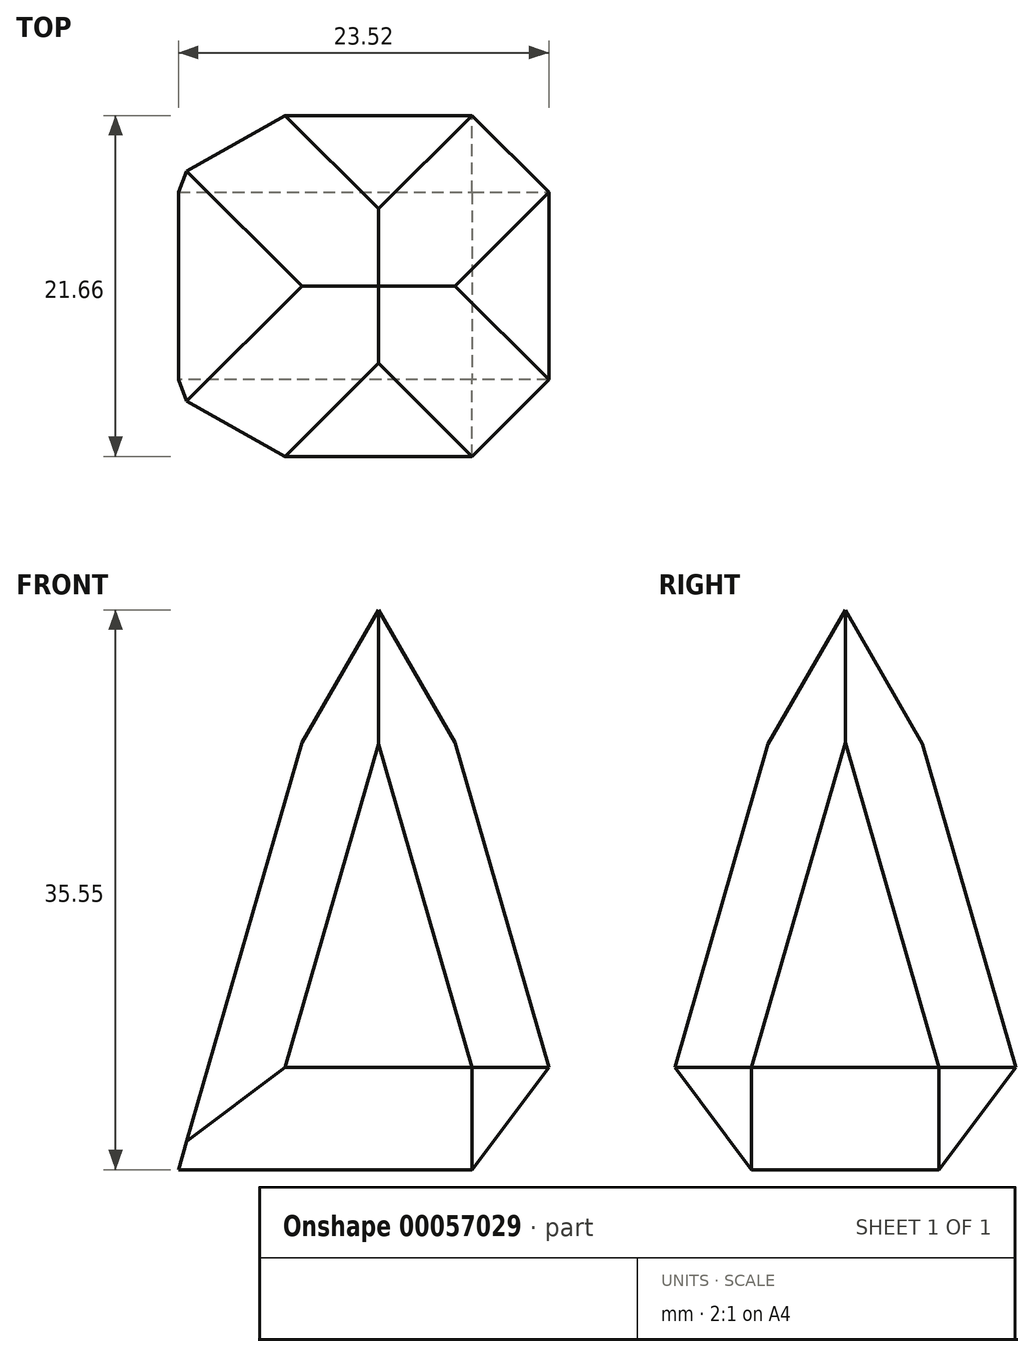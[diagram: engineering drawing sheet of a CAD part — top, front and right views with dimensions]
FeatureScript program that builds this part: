
annotation { "Feature Type Name" : "Feature", "Feature Type Description" : "" }
export const myFeature = defineFeature(function(context is Context, id is Id, definition is map)
    precondition{}
    {
        {
            var Q0;
            Q0=qCreatedBy(makeId("Front.planeOp"),FACE);
            var sketch = newSketch(context, id + "F0", { "sketchPlane" : qUnion([Q0])});
            skLineSegment(sketch, "E0", {"start": v(-12.7, 0) * mm, "end": v(12.7, 0) * mm});
            skLineSegment(sketch, "E1", {"start": v(12.7, 0) * mm, "end": v(0, 43.94) * mm});
            skLineSegment(sketch, "E2", {"start": v(0, 43.94) * mm, "end": v(-12.7, 0) * mm});
            skSolve(sketch);
        }
        {
            var Q0;
            Q0 = qSketchRegion(id + "F0", true);
            extrude(context, id + "F1", {"entities" : qUnion([Q0]), "depth" : 25.4 * mm});
        }
        {
            var Q0;
            Q0=qCreatedBy(makeId("Right.planeOp"),FACE);
            var sketch = newSketch(context, id + "F2", { "sketchPlane" : qUnion([Q0])});
            skLineSegment(sketch, "E3", {"start": v(0, 0) * mm, "end": v(0, 44.07) * mm});
            skLineSegment(sketch, "E4", {"start": v(0, 44.07) * mm, "end": v(-25.4, 44.07) * mm});
            skLineSegment(sketch, "E5", {"start": v(-25.4, 44.07) * mm, "end": v(-25.4, 0) * mm});
            skLineSegment(sketch, "E6", {"start": v(-25.4, 0) * mm, "end": v(-12.7, 44.07) * mm});
            skLineSegment(sketch, "E7", {"start": v(-12.7, 44.07) * mm, "end": v(0, 0) * mm});
            skSolve(sketch);
        }
        {
            var Q0;
            Q0 = qSketchRegion(id + "F2", true);
            extrude(context, id + "F3", {"entities" : qUnion([Q0]), "operationType" : NewBodyOperationType.REMOVE, "depth" : 25.4 * mm, "hasSecondDirection" : true, "secondDirectionOppositeDirection" : true, "secondDirectionDepth" : 25.4 * mm});
        }
        {
            var Q0;
            Q0=makeQuery(id+"F3.boolean.opBoolean","INTERSECT",EDGE,{"derivedFrom":[makeQuery(id+"F1.opExtrude","SWEPT_FACE",FACE,{"disambiguationData":[OSD([sQuery(id+"F0.wireOp",EDGE,"E1")])]}),makeQuery(id+"F3.opExtrude","SWEPT_FACE",FACE,{"disambiguationData":[OSD([sQuery(id+"F2.wireOp",EDGE,"E7")])]})]});
            var Q1;
            Q1=makeQuery(id+"F3.boolean.opBoolean","INTERSECT",EDGE,{"derivedFrom":[makeQuery(id+"F1.opExtrude","SWEPT_FACE",FACE,{"disambiguationData":[OSD([sQuery(id+"F0.wireOp",EDGE,"E2")])]}),makeQuery(id+"F3.opExtrude","SWEPT_FACE",FACE,{"disambiguationData":[OSD([sQuery(id+"F2.wireOp",EDGE,"E6")])]})]});
            var Q2;
            Q2=makeQuery(id+"F3.boolean.opBoolean","INTERSECT",EDGE,{"derivedFrom":[makeQuery(id+"F1.opExtrude","SWEPT_FACE",FACE,{"disambiguationData":[OSD([sQuery(id+"F0.wireOp",EDGE,"E2")])]}),makeQuery(id+"F3.opExtrude","SWEPT_FACE",FACE,{"disambiguationData":[OSD([sQuery(id+"F2.wireOp",EDGE,"E7")])]})]});
            var Q3;
            Q3=makeQuery(id+"F1.opExtrude","SWEPT_EDGE",EDGE,{"disambiguationData":[OSD([sQuery(id+"F0.wireOp",EDGE,"E0"),sQuery(id+"F0.wireOp",EDGE,"E1")])]});
            var Q4;
            Q4=makeQuery(id+"F3.boolean.opBoolean","MERGE",EDGE,{"derivedFrom":[makeQuery(id+"F1.opExtrude","CAP_EDGE",EDGE,{"disambiguationData":[OSD([sQuery(id+"F0.wireOp",EDGE,"E0")])],"isStart":false}),makeQuery(id+"F3.opExtrude","SWEPT_EDGE",EDGE,{"disambiguationData":[OSD([sQuery(id+"F2.wireOp",EDGE,"E5"),sQuery(id+"F2.wireOp",EDGE,"E6")])]})]});
            var Q5;
            Q5=makeQuery(id+"F3.boolean.opBoolean","MERGE",EDGE,{"derivedFrom":[makeQuery(id+"F1.opExtrude","CAP_EDGE",EDGE,{"disambiguationData":[OSD([sQuery(id+"F0.wireOp",EDGE,"E0")])],"isStart":true}),makeQuery(id+"F3.opExtrude","SWEPT_EDGE",EDGE,{"disambiguationData":[OSD([sQuery(id+"F2.wireOp",EDGE,"E3"),sQuery(id+"F2.wireOp",EDGE,"E7")])]})]});
            var Q6;
            Q6=makeQuery(id+"F3.boolean.opBoolean","INTERSECT",EDGE,{"derivedFrom":[makeQuery(id+"F1.opExtrude","SWEPT_FACE",FACE,{"disambiguationData":[OSD([sQuery(id+"F0.wireOp",EDGE,"E1")])]}),makeQuery(id+"F3.opExtrude","SWEPT_FACE",FACE,{"disambiguationData":[OSD([sQuery(id+"F2.wireOp",EDGE,"E6")])]})]});
            chamfer(context, id + "F4", {"entities" : qUnion([Q0, Q1, Q2, Q3, Q4, Q5, Q6]), "width" : 5.08 * mm, "tangentPropagation" : true});
        }
    });
